# Revit family: 1.1 Вентиляторы KORF ANR V2
name_source: partatom
category: Оборудование
revit_build: Autodesk Revit 2016 (Build: 20151209_0715(x64)
units: mm (PartAtom-declared; Revit-internal decimal feet)

## family parameters
Всегда вертикально = Да
На основе рабочей плоскости = Нет
Общий = Нет
При загрузке вырезать с полостями = Нет
Размер круглого соединителя = Использовать диаметр
Тип детали = Нормальный
Точка расчета площади = Нет

## types (26) — shared parameters
h = 130 мм
Единица измерения = шт.
Завод изготовитель = KORF
Ключевая пометка = Вентиляция
Раздел = ОВ
Синий = Синий
высота ножек = 120 мм

## per-type parameters (varying)
| type | А | А1 | Б | Б1 | Высота | Д | Д1 | Материал | Наименование и тех.хар-ка | Середина | Ширина | привязка значка |
| ANR 6 V2.0. | 1100 мм | 1080 мм | 1100 мм | 1080 мм | 1025 мм | 1100 мм | 1080 мм | Сталь серая | Секция вентилятора короткая с назад загнутыми лопатками и выбросом вверх | 670 мм | 1025 мм | 550 мм |
| ANR 7 V2.0. | 1100 мм | 1080 мм | 1320 мм | 1300 мм | 1025 мм | 1100 мм | 1080 мм | Сталь серая | Секция вентилятора короткая с назад загнутыми лопатками и выбросом вверх | 780 мм | 1025 мм | 660 мм |
| ANR 8 V2.0. | 1320 мм | 1300 мм | 1320 мм | 1300 мм | 1245 мм | 1100 мм | 1080 мм | Сталь серая | Секция вентилятора короткая с назад загнутыми лопатками и выбросом вверх | 780 мм | 1025 мм | 660 мм |
| ANR 12 V2.0. | 1435 мм | 1415 мм | 1435 мм | 1415 мм | 1360 мм | 1100 мм | 1080 мм | Сталь серая | Секция вентилятора короткая с назад загнутыми лопатками и выбросом вверх | 838 мм | 1025 мм | 718 мм |
| ANR 20 V2.0. | 1660 мм | 1640 мм | 1660 мм | 1640 мм | 1585 мм | 1100 мм | 1080 мм | Сталь серая | Секция вентилятора короткая с назад загнутыми лопатками и выбросом вверх | 950 мм | 1025 мм | 830 мм |
| ANR 25 V2.0. | 2045 мм | 2025 мм | 2045 мм | 2025 мм | 1970 мм | 1100 мм | 1080 мм | Сталь серая | Секция вентилятора короткая с назад загнутыми лопатками и выбросом вверх | 1143 мм | 1025 мм | 1023 мм |
| ANR 30 V2.1. | 2485 мм | 2465 мм | 2045 мм | 2025 мм | 2410 мм | 1625 мм | 1605 мм | Сталь серая | Секция вентилятора удлиненная кдлиненная с назад загнутыми лопатками и выбросом вверх | 1143 мм | 1550 мм | 1023 мм |
| ANR 35 V2.1. | 2485 мм | 2465 мм | 2485 мм | 2465 мм | 2410 мм | 2150 мм | 2130 мм | Сталь серая | Секция вентилятора удлиненная с назад загнутыми лопатками и выбросом вверх | 1363 мм | 2075 мм | 1243 мм |
| ANR 40 V2.1. | 3320 мм | 3300 мм | 3320 мм | 3300 мм | 3245 мм | 1625 мм | 1605 мм | Сталь серая | Секция вентилятора удлиненная с назад загнутыми лопатками и выбросом вверх | 1780 мм | 1550 мм | 1660 мм |
| ANR 45 V2.1. | 3320 мм | 3300 мм | 4090 мм | 4070 мм | 3245 мм | 1625 мм | 1605 мм | Сталь серая | Секция вентилятора удлиненная с назад загнутыми лопатками и выбросом вверх | 2165 мм | 1550 мм | 2045 мм |
| ANR 6 V2.1. | 1100 мм | 1080 мм | 1100 мм | 1080 мм | 1025 мм | 1625 мм | 1605 мм | Сталь серая | Секция вентилятора удлиненная с назад загнутыми лопатками и выбросом вверх | 670 мм | 1550 мм | 550 мм |
| ANR 6 V2.2. | 1100 мм | 1080 мм | 1100 мм | 1080 мм | 1025 мм | 1625 мм | 1605 мм | Сталь серая | Секция вентилятора длинная с назад загнутыми лопатками и выбросом вверх | 670 мм | 1550 мм | 550 мм |
| ANR 7 V2.1. | 1100 мм | 1080 мм | 1320 мм | 1300 мм | 1025 мм | 1625 мм | 1605 мм | Сталь серая | Секция вентилятора удлиненная с назад загнутыми лопатками и выбросом вверх | 780 мм | 1550 мм | 660 мм |
| ANR 7 V2.2. | 1100 мм | 1080 мм | 1320 мм | 1300 мм | 1025 мм | 1625 мм | 1605 мм | Сталь серая | Секция вентилятора длинная с назад загнутыми лопатками и выбросом вверх | 780 мм | 1550 мм | 660 мм |
| ANR 8 V2.1. | 1320 мм | 1300 мм | 1320 мм | 1300 мм | 1245 мм | 1625 мм | 1605 мм | Сталь серая | Секция вентилятора удлиненная с назад загнутыми лопатками и выбросом вверх | 780 мм | 1550 мм | 660 мм |
| ANR 8 V2.2. | 1320 мм | 1300 мм | 1320 мм | 1300 мм | 1245 мм | 1625 мм | 1605 мм | Сталь серая | Секция вентилятора длинная с назад загнутыми лопатками и выбросом вверх | 780 мм | 1550 мм | 660 мм |
| ANR 12 V2.1. | 1435 мм | 1415 мм | 1435 мм | 1415 мм | 1360 мм | 1625 мм | 1605 мм | Сталь серая | Секция вентилятора удлиненная с назад загнутыми лопатками и выбросом вверх | 838 мм | 1550 мм | 718 мм |
| ANR 12 V2.2. | 1435 мм | 1415 мм | 1435 мм | 1415 мм | 1360 мм | 1625 мм | 1605 мм | Сталь серая | Секция вентилятора длинная с назад загнутыми лопатками и выбросом вверх | 838 мм | 1550 мм | 718 мм |
| ANR 20 V2.1. | 1660 мм | 1640 мм | 1660 мм | 1640 мм | 1585 мм | 1625 мм | 1605 мм | Сталь серая | Секция вентилятора удлиненная с назад загнутыми лопатками и выбросом вверх | 950 мм | 1550 мм | 830 мм |
| ANR 20 V2.2. | 1660 мм | 1640 мм | 1660 мм | 1640 мм | 1585 мм | 1625 мм | 1605 мм | Сталь серая | Секция вентилятора удлиненная с назад загнутыми лопатками и выбросом вверх | 950 мм | 1550 мм | 830 мм |
| ANR 25 V2.1. | 2045 мм | 2025 мм | 2045 мм | 2025 мм | 1970 мм | 1625 мм | 1605 мм | Сталь серая | Секция вентилятора удлиненная с назад загнутыми лопатками и выбросом вверх | 1143 мм | 1550 мм | 1023 мм |
| ANR 25 V2.2. | 2045 мм | 2025 мм | 2045 мм | 2025 мм | 1970 мм | 1625 мм | 1605 мм | Сталь серая | Секция вентилятора длинная с назад загнутыми лопатками и выбросом вверх | 1143 мм | 1550 мм | 1023 мм |
| ANR 30 V2.2. | 2485 мм | 2465 мм | 2045 мм | 2025 мм | 2410 мм | 1625 мм | 1605 мм | Сталь серая | Секция вентилятора длинная кдлиненная с назад загнутыми лопатками и выбросом вверх | 1143 мм | 1550 мм | 1023 мм |
| ANR 35 V2.2. | 2485 мм | 2465 мм | 2485 мм | 2465 мм | 2410 мм | 2150 мм | 2130 мм | Сталь серая | Секция вентилятора длинная с назад загнутыми лопатками и выбросом вверх | 1363 мм | 2075 мм | 1243 мм |
| ANR 40 V2.2. | 3320 мм | 3300 мм | 3320 мм | 3300 мм | 3245 мм | 1625 мм | 1605 мм | Сталь серая | Секция вентилятора длинная с назад загнутыми лопатками и выбросом вверх | 1780 мм | 1550 мм | 1660 мм |
| ANR 45 V2.2. | 3320 мм | 3300 мм | 4090 мм | 4070 мм | 3245 мм | 1625 мм | 1605 мм | RAL 0000 Серый металл | Секция вентилятора длинная с назад загнутыми лопатками и выбросом вверх | 2165 мм | 1550 мм | 2045 мм |

note: column(s) folded — value = type name in every type: Тип, марка, обозначение
